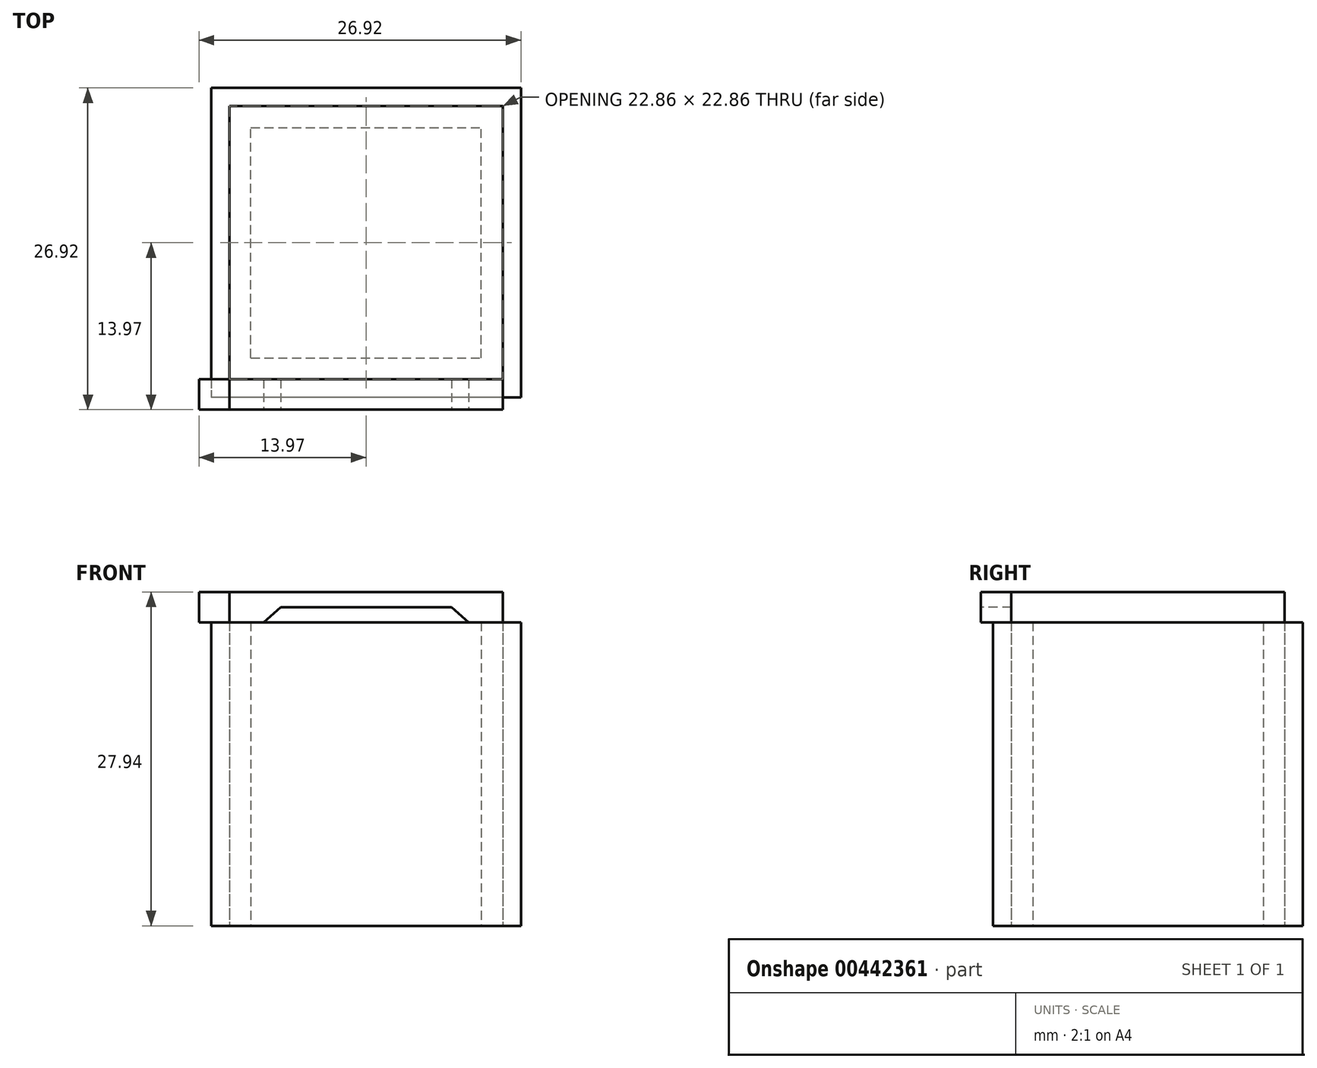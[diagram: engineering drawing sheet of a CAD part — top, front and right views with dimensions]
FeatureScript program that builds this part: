
annotation { "Feature Type Name" : "Feature", "Feature Type Description" : "" }
export const myFeature = defineFeature(function(context is Context, id is Id, definition is map)
    precondition{}
    {
        {
            var Q0;
            Q0=qCreatedBy(makeId("Top.planeOp"),FACE);
            var sketch = newSketch(context, id + "F0", { "sketchPlane" : qUnion([Q0])});
            skLineSegment(sketch, "E0", {"start": v(0, 0) * mm, "end": v(0, 22.86) * mm});
            skLineSegment(sketch, "E1", {"start": v(0, 22.86) * mm, "end": v(-22.86, 22.86) * mm});
            skLineSegment(sketch, "E2", {"start": v(-22.86, 22.86) * mm, "end": v(-22.86, 0) * mm});
            skLineSegment(sketch, "E3", {"start": v(-22.86, 0) * mm, "end": v(0, 0) * mm});
            skLineSegment(sketch, "E4", {"start": v(-24.38, 24.38) * mm, "end": v(-24.38, -1.52) * mm});
            skLineSegment(sketch, "E5", {"start": v(1.52, -1.52) * mm, "end": v(1.52, 24.38) * mm});
            skLineSegment(sketch, "E6", {"start": v(-24.38, 24.38) * mm, "end": v(1.52, 24.38) * mm});
            skLineSegment(sketch, "E7", {"start": v(1.52, -1.52) * mm, "end": v(-24.38, -1.52) * mm});
            skSolve(sketch);
        }
        {
            var Q0;
            Q0 = qSketchRegion(id + "F0", true);
            extrude(context, id + "F1", {"entities" : qUnion([Q0]), "depth" : 25.4 * mm});
        }
        {
            var Q0;
            Q0=makeQuery(id+"F0.imprint","IMPRINT",FACE,{"disambiguationData":[TD([[makeQuery(id+"F0.imprint","IMPRINT",EDGE,{"derivedFrom":sQuery(id+"F0.wireOp",EDGE,"E0")}),1.0]])]});
            extrude(context, id + "F2", {"entities" : qUnion([Q0]), "depth" : 27.94 * mm});
        }
        {
            var Q0;
            Q0=makeQuery(id+"F2.opExtrude","SWEPT_FACE",FACE,{"disambiguationData":[OSD([sQuery(id+"F0.wireOp",EDGE,"E3")])]});
            var sketch = newSketch(context, id + "F3", { "sketchPlane" : qUnion([Q0])});
            skLineSegment(sketch, "E8.bottom", {"start": v(-22.86, 27.94) * mm, "end": v(0, 27.94) * mm});
            skLineSegment(sketch, "E8.top", {"start": v(-22.86, 25.4) * mm, "end": v(0, 25.4) * mm});
            skLineSegment(sketch, "E8.left", {"start": v(-22.86, 27.94) * mm, "end": v(-22.86, 25.4) * mm});
            skLineSegment(sketch, "E8.right", {"start": v(0, 27.94) * mm, "end": v(0, 25.4) * mm});
            skSolve(sketch);
        }
        {
            var Q0;
            Q0 = qSketchRegion(id + "F3", true);
            extrude(context, id + "F4", {"entities" : qUnion([Q0]), "depth" : 2.54 * mm});
        }
        {
            var Q0;
            Q0=makeQuery(id+"F4.opExtrude","SWEPT_FACE",FACE,{"disambiguationData":[OSD([sQuery(id+"F3.wireOp",EDGE,"E8.left")])]});
            var sketch = newSketch(context, id + "F5", { "sketchPlane" : qUnion([Q0])});
            skLineSegment(sketch, "E9.bottom", {"start": v(0, 27.94) * mm, "end": v(2.54, 27.94) * mm});
            skLineSegment(sketch, "E9.top", {"start": v(0, 25.4) * mm, "end": v(2.54, 25.4) * mm});
            skLineSegment(sketch, "E9.left", {"start": v(0, 27.94) * mm, "end": v(0, 25.4) * mm});
            skLineSegment(sketch, "E9.right", {"start": v(2.54, 27.94) * mm, "end": v(2.54, 25.4) * mm});
            skSolve(sketch);
        }
        {
            var Q0;
            Q0 = qSketchRegion(id + "F5", true);
            extrude(context, id + "F6", {"entities" : qUnion([Q0]), "depth" : 2.54 * mm});
        }
        {
            var Q0;
            Q0=makeQuery(id+"F4.opExtrude","CAP_FACE",FACE,{"disambiguationData":[OSD([sQuery(id+"F3.wireOp",EDGE,"E8.bottom"),sQuery(id+"F3.wireOp",EDGE,"E8.top"),sQuery(id+"F3.wireOp",EDGE,"E8.left"),sQuery(id+"F3.wireOp",EDGE,"E8.right")])],"isStart":false});
            var sketch = newSketch(context, id + "F7", { "sketchPlane" : qUnion([Q0])});
            skLineSegment(sketch, "E10", {"start": v(-17.14, 27.94) * mm, "end": v(-5.72, 27.94) * mm});
            skPoint(sketch, "E11.startSnap0", {"position": v(-11.43, 27.94) * mm});
            skPoint(sketch, "E11.startSnap1", {"position": v(-22.86, 26.67) * mm});
            skLineSegment(sketch, "E12", {"start": v(-20, 25.4) * mm, "end": v(-17.14, 27.94) * mm});
            skLineSegment(sketch, "E13", {"start": v(-2.86, 25.4) * mm, "end": v(-5.71, 27.94) * mm});
            skLineSegment(sketch, "E14", {"start": v(-20, 25.4) * mm, "end": v(-2.86, 25.4) * mm});
            skLineSegment(sketch, "E15", {"start": v(-18.57, 26.67) * mm, "end": v(-4.29, 26.67) * mm});
            skSolve(sketch);
        }
        {
            var Q0;
            {var subQ0=sQuery(id+"F7.wireOp",EDGE,"E14");Q0=makeQuery(id+"F7.imprint","IMPRINT",FACE,{"disambiguationData":[TD([[makeQuery(id+"F7.imprint","IMPRINT",EDGE,{"derivedFrom":subQ0}),1.0]])]});}
            extrude(context, id + "F8", {"entities" : qUnion([Q0]), "operationType" : NewBodyOperationType.REMOVE, "oppositeDirection" : true, "depth" : 2.54 * mm});
        }
        {
            var Q0;
            Q0=makeQuery(id+"F2.opExtrude","CAP_FACE",FACE,{"disambiguationData":[OSD([sQuery(id+"F0.wireOp",EDGE,"E0"),sQuery(id+"F0.wireOp",EDGE,"E1"),sQuery(id+"F0.wireOp",EDGE,"E2"),sQuery(id+"F0.wireOp",EDGE,"E3")])],"isStart":true});
            var sketch = newSketch(context, id + "F9", { "sketchPlane" : qUnion([Q0])});
            skLineSegment(sketch, "E16", {"start": v(-22.86, 0) * mm, "end": v(-21.06, -1.8) * mm});
            skLineSegment(sketch, "E17", {"start": v(-21.06, -1.8) * mm, "end": v(-21.06, -22.86) * mm});
            skLineSegment(sketch, "E18", {"start": v(-22.86, -22.86) * mm, "end": v(-21.06, -21.06) * mm});
            skLineSegment(sketch, "E19", {"start": v(-21.06, -21.06) * mm, "end": v(0, -21.06) * mm});
            skLineSegment(sketch, "E20", {"start": v(-21.06, -1.8) * mm, "end": v(0, -1.8) * mm});
            skLineSegment(sketch, "E21", {"start": v(0, 0) * mm, "end": v(-1.81, -1.8) * mm});
            skLineSegment(sketch, "E22", {"start": v(-1.81, -1.8) * mm, "end": v(-1.81, -21.06) * mm});
            skSolve(sketch);
        }
        {
            var Q0;
            Q0 = qSketchRegion(id + "F9", true);
            extrude(context, id + "F10", {"entities" : qUnion([Q0]), "operationType" : NewBodyOperationType.REMOVE, "oppositeDirection" : true, "depth" : 25.4 * mm});
        }
    });
